# Revit family: 306_79b931d294f041bc8e3cd95bca595d
name_source: partatom
category: Pipe Accessories
units: mm (PartAtom-declared; Revit-internal decimal feet)

## family parameters
Always vertical = Yes
Cut with Voids When Loaded = No
Part Type = Valve - Breaks Into
Round Connector Dimension = Use Diameter
Shared = No
Work Plane-Based = No

## types (6) — shared parameters
B = 50 mm  [stored 0.164042 ft]
C = 60 mm  [stored 0.19685 ft]
CAT0 = Yes
CT2 = 24 mm  [stored 0.0787402 ft]
Description = Thermostatic mixing valve VTA552, PN10 external thread
L2D = 64 mm
L2D_Min = 3048 mm  [stored 10 ft]
LT2 = 32 mm  [stored 0.104987 ft]
MC = No
Manufacturer = ESBE
QmdConnectorList = 301;D;302;D
URL = http://www.esbe.eu
W1 = 21 mm  [stored 0.0688976 ft]
WT2 = 28 mm  [stored 0.0918635 ft]
X1 = 2 mm  [stored 0.00656168 ft]
X3 = 60 mm  [stored 0.19685 ft]
X4 = 54 mm  [stored 0.177165 ft]
X6 = 10 mm  [stored 0.0328084 ft]
magiPartTypeId = 306
magiProductFamilyId = 79b931d294f041bc8e3cd95bca595d

## per-type parameters (varying)
| type | A | A__ve | D | DT2 | R2 | W2D | Z1 | Z1__ve | Z2 | magiProductId |
| VTA552 20-43°C G1 1/4-3,5 | 38 mm | -38 mm  [stored -0.124672 ft] | 32 mm | 16 mm  [stored 0.0524934 ft] | 14 mm  [stored 0.0459318 ft] | 32 mm  [stored 0.104987 ft] | 14 mm  [stored 0.0459318 ft] | -14 mm  [stored -0.0459318 ft] | 6 mm  [stored 0.019685 ft] | b683b850debb4f4baa990f424427b6 |
| VTA552 50-75°C G1-3,2 | 35 mm  [stored 0.114829 ft] | -35 mm  [stored -0.114829 ft] | 25 mm | 13 mm  [stored 0.0426509 ft] | 11 mm  [stored 0.0360892 ft] | 25 mm  [stored 0.082021 ft] | 16 mm  [stored 0.0524934 ft] | -16 mm  [stored -0.0524934 ft] | 7 mm  [stored 0.0229659 ft] | 4252d59b15bc4af48e4443d8d991be |
| VTA552 50-75°C G1 1/4-3,5 | 38 mm | -38 mm  [stored -0.124672 ft] | 32 mm | 16 mm  [stored 0.0524934 ft] | 14 mm  [stored 0.0459318 ft] | 32 mm  [stored 0.104987 ft] | 14 mm  [stored 0.0459318 ft] | -14 mm  [stored -0.0459318 ft] | 6 mm  [stored 0.019685 ft] | e56208b9dc1b4cf1919d51a3383f1e |
| VTA552 45-65°C G1-3,2 | 35 mm  [stored 0.114829 ft] | -35 mm  [stored -0.114829 ft] | 25 mm | 13 mm  [stored 0.0426509 ft] | 11 mm  [stored 0.0360892 ft] | 25 mm  [stored 0.082021 ft] | 16 mm  [stored 0.0524934 ft] | -16 mm  [stored -0.0524934 ft] | 7 mm  [stored 0.0229659 ft] | 659b96c9f0fc4c9d94732eb8b7d212 |
| VTA552 45-65°C G1 1/4-3,5 | 38 mm | -38 mm  [stored -0.124672 ft] | 32 mm | 16 mm  [stored 0.0524934 ft] | 14 mm  [stored 0.0459318 ft] | 32 mm  [stored 0.104987 ft] | 14 mm  [stored 0.0459318 ft] | -14 mm  [stored -0.0459318 ft] | 6 mm  [stored 0.019685 ft] | bd8a4231302943098b1d2b89f6b1b1 |
| VTA552 20-43°C G1-3,2 | 35 mm  [stored 0.114829 ft] | -35 mm  [stored -0.114829 ft] | 25 mm | 13 mm  [stored 0.0426509 ft] | 11 mm  [stored 0.0360892 ft] | 25 mm  [stored 0.082021 ft] | 16 mm  [stored 0.0524934 ft] | -16 mm  [stored -0.0524934 ft] | 7 mm  [stored 0.0229659 ft] | 788b30dcbe804c42b118ec37b44a46 |

note: column(s) folded — value = type name in every type: magiProductCode

note: [stored X ft] marks values corroborated as IEEE doubles in the binary element streams (Revit-internal decimal feet)

## geometry (parser evidence)
native form markers: Sweep x1
no freeform markers — native parametric forms only
